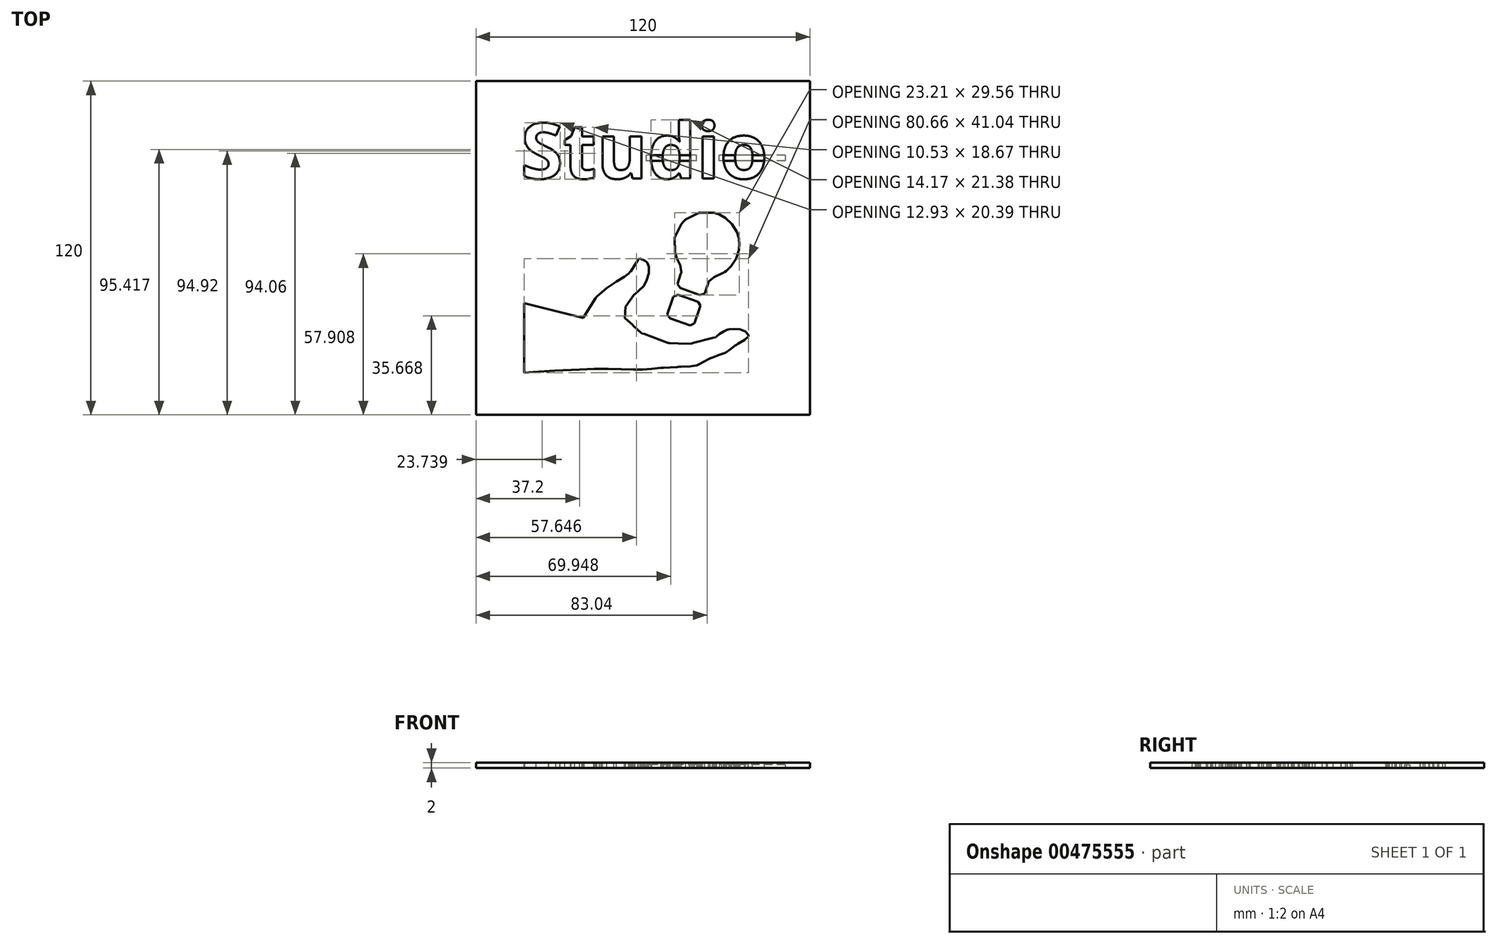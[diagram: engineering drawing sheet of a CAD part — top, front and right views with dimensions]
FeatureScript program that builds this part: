
annotation { "Feature Type Name" : "Feature", "Feature Type Description" : "" }
export const myFeature = defineFeature(function(context is Context, id is Id, definition is map)
    precondition{}
    {
        {
            var Q0;
            Q0=qCreatedBy(makeId("Top.planeOp"),FACE);
            var sketch = newSketch(context, id + "F0", { "sketchPlane" : qUnion([Q0])});
            skLineSegment(sketch, "E0.bottom", {"start": v(-61, 60) * mm, "end": v(59, 60) * mm});
            skLineSegment(sketch, "E0.top", {"start": v(-61, -60) * mm, "end": v(59, -60) * mm});
            skLineSegment(sketch, "E0.left", {"start": v(-61, 60) * mm, "end": v(-61, -60) * mm});
            skLineSegment(sketch, "E0.right", {"start": v(59, 60) * mm, "end": v(59, -60) * mm});
            skSolve(sketch);
        }
        {
            var Q0;
            Q0=qSketchRegion(id+"F0",true);
            extrude(context, id + "F1", {"entities" : qUnion([Q0]), "depth" : 2 * mm});
        }
        {
            var Q0;
            Q0=makeQuery(id+"F1.opExtrude","CAP_FACE",FACE,{"disambiguationData":[OSD([sQuery(id+"F0.wireOp",EDGE,"E0.bottom"),sQuery(id+"F0.wireOp",EDGE,"E0.top"),sQuery(id+"F0.wireOp",EDGE,"E0.left"),sQuery(id+"F0.wireOp",EDGE,"E0.right")])],"isStart":false});
            var sketch = newSketch(context, id + "F2", { "sketchPlane" : qUnion([Q0])});
            skText(sketch, "E1", { "text": "Studio", "fontName": "OpenSans-Bold.ttf"});
            const initialGuessF2  = {"E1": [-0.045, 0.025, 1, 0, 0.02]};
            skSetInitialGuess(sketch, initialGuessF2);
            skSolve(sketch);
        }
        {
            var Q0;
            Q0=qSketchRegion(id+"F2",true);
            extrude(context, id + "F3", {"entities" : qUnion([Q0]), "operationType" : NewBodyOperationType.REMOVE, "oppositeDirection" : true, "depth" : 25 * mm});
        }
        {
            var Q0;
            {var subQ0=sQuery(id+"F0.wireOp",EDGE,"E0.top");var subQ1=sQuery(id+"F0.wireOp",EDGE,"E0.right");var subQ2=sQuery(id+"F0.wireOp",EDGE,"E0.bottom");var subQ3=sQuery(id+"F0.wireOp",EDGE,"E0.left");Q0=makeQuery(id+"F3.boolean.opBoolean","SPLIT",FACE,{"disambiguationData":[TD([makeQuery(id+"F1.opExtrude","SWEPT_FACE",FACE,{"disambiguationData":[OSD([subQ2])]})])],"derivedFrom":makeQuery(id+"F1.opExtrude","CAP_FACE",FACE,{"disambiguationData":[OSD([subQ2,subQ0,subQ3,subQ1])],"isStart":false})});}
            var sketch = newSketch(context, id + "F4", { "sketchPlane" : qUnion([Q0])});
            skLineSegment(sketch, "E2", {"start": v(-43.68, -19.85) * mm, "end": v(-43.68, -44.85) * mm});
            skLineSegment(sketch, "E3", {"start": v(-43.68, -44.85) * mm, "end": v(-40.4, -44.62) * mm});
            skLineSegment(sketch, "E4", {"start": v(-40.4, -44.62) * mm, "end": v(-32.66, -44.12) * mm});
            skLineSegment(sketch, "E5", {"start": v(-32.66, -44.12) * mm, "end": v(-23.76, -43.64) * mm});
            skLineSegment(sketch, "E6", {"start": v(-23.76, -43.64) * mm, "end": v(-18.48, -43.42) * mm});
            skLineSegment(sketch, "E7", {"start": v(-18.48, -43.42) * mm, "end": v(-16.9, -43.43) * mm});
            skLineSegment(sketch, "E8", {"start": v(-16.9, -43.43) * mm, "end": v(-16.04, -43.43) * mm});
            skLineSegment(sketch, "E9", {"start": v(-16.04, -43.43) * mm, "end": v(-13.48, -43.48) * mm});
            skLineSegment(sketch, "E10", {"start": v(-13.48, -43.48) * mm, "end": v(-8.78, -43.57) * mm});
            skLineSegment(sketch, "E11", {"start": v(-8.78, -43.57) * mm, "end": v(-4.34, -43.65) * mm});
            skLineSegment(sketch, "E12", {"start": v(-4.34, -43.65) * mm, "end": v(-2.09, -43.67) * mm});
            skLineSegment(sketch, "E13", {"start": v(-2.09, -43.67) * mm, "end": v(-1.65, -43.66) * mm});
            skLineSegment(sketch, "E14", {"start": v(-1.65, -43.66) * mm, "end": v(-1.15, -43.64) * mm});
            skLineSegment(sketch, "E15", {"start": v(-1.15, -43.64) * mm, "end": v(2.17, -43.39) * mm});
            skLineSegment(sketch, "E16", {"start": v(2.17, -43.39) * mm, "end": v(5.45, -43.1) * mm});
            skLineSegment(sketch, "E17", {"start": v(5.45, -43.1) * mm, "end": v(5.93, -43.06) * mm});
            skLineSegment(sketch, "E18", {"start": v(5.93, -43.06) * mm, "end": v(6.4, -43.02) * mm});
            skLineSegment(sketch, "E19", {"start": v(6.4, -43.02) * mm, "end": v(8.69, -42.9) * mm});
            skLineSegment(sketch, "E20", {"start": v(8.69, -42.9) * mm, "end": v(11.26, -42.76) * mm});
            skLineSegment(sketch, "E21", {"start": v(11.26, -42.76) * mm, "end": v(11.88, -42.72) * mm});
            skLineSegment(sketch, "E22", {"start": v(11.88, -42.72) * mm, "end": v(12.7, -42.65) * mm});
            skLineSegment(sketch, "E23", {"start": v(12.7, -42.65) * mm, "end": v(15.93, -42.51) * mm});
            skLineSegment(sketch, "E24", {"start": v(15.93, -42.51) * mm, "end": v(18.43, -42.11) * mm});
            skLineSegment(sketch, "E25", {"start": v(18.43, -42.11) * mm, "end": v(18.89, -41.92) * mm});
            skLineSegment(sketch, "E26", {"start": v(18.89, -41.92) * mm, "end": v(19.2, -41.79) * mm});
            skLineSegment(sketch, "E27", {"start": v(19.2, -41.79) * mm, "end": v(20.81, -40.9) * mm});
            skLineSegment(sketch, "E28", {"start": v(20.81, -40.9) * mm, "end": v(22.77, -39.85) * mm});
            skLineSegment(sketch, "E29", {"start": v(22.77, -39.85) * mm, "end": v(23.24, -39.65) * mm});
            skLineSegment(sketch, "E30", {"start": v(23.24, -39.65) * mm, "end": v(23.92, -39.34) * mm});
            skLineSegment(sketch, "E31", {"start": v(23.92, -39.34) * mm, "end": v(26.56, -38.33) * mm});
            skLineSegment(sketch, "E32", {"start": v(26.56, -38.33) * mm, "end": v(28.37, -37.7) * mm});
            skLineSegment(sketch, "E33", {"start": v(28.37, -37.7) * mm, "end": v(28.64, -37.59) * mm});
            skLineSegment(sketch, "E34", {"start": v(28.64, -37.59) * mm, "end": v(28.9, -37.46) * mm});
            skLineSegment(sketch, "E35", {"start": v(28.9, -37.46) * mm, "end": v(30.31, -36.44) * mm});
            skLineSegment(sketch, "E36", {"start": v(30.31, -36.44) * mm, "end": v(32.13, -35.05) * mm});
            skLineSegment(sketch, "E37", {"start": v(32.13, -35.05) * mm, "end": v(32.6, -34.75) * mm});
            skLineSegment(sketch, "E38", {"start": v(32.6, -34.75) * mm, "end": v(33.06, -34.44) * mm});
            skLineSegment(sketch, "E39", {"start": v(33.06, -34.44) * mm, "end": v(35.54, -32.97) * mm});
            skLineSegment(sketch, "E40", {"start": v(35.54, -32.97) * mm, "end": v(36.98, -31.77) * mm});
            skLineSegment(sketch, "E41", {"start": v(36.98, -31.77) * mm, "end": v(36.92, -31.6) * mm});
            skLineSegment(sketch, "E42", {"start": v(36.92, -31.6) * mm, "end": v(36.75, -31.13) * mm});
            skLineSegment(sketch, "E43", {"start": v(36.75, -31.13) * mm, "end": v(35.73, -29.93) * mm});
            skLineSegment(sketch, "E44", {"start": v(35.73, -29.93) * mm, "end": v(33.88, -29.17) * mm});
            skLineSegment(sketch, "E45", {"start": v(33.88, -29.17) * mm, "end": v(31.66, -29.06) * mm});
            skLineSegment(sketch, "E46", {"start": v(31.66, -29.06) * mm, "end": v(29.93, -29.27) * mm});
            skLineSegment(sketch, "E47", {"start": v(29.93, -29.27) * mm, "end": v(29.37, -29.38) * mm});
            skLineSegment(sketch, "E48", {"start": v(29.37, -29.38) * mm, "end": v(29, -29.45) * mm});
            skLineSegment(sketch, "E49", {"start": v(29, -29.45) * mm, "end": v(28, -29.95) * mm});
            skLineSegment(sketch, "E50", {"start": v(28, -29.95) * mm, "end": v(26.57, -30.9) * mm});
            skLineSegment(sketch, "E51", {"start": v(26.57, -30.9) * mm, "end": v(25.44, -31.77) * mm});
            skLineSegment(sketch, "E52", {"start": v(25.44, -31.77) * mm, "end": v(24.98, -32.17) * mm});
            skLineSegment(sketch, "E53", {"start": v(24.98, -32.17) * mm, "end": v(24.27, -32.3) * mm});
            skLineSegment(sketch, "E54", {"start": v(24.27, -32.3) * mm, "end": v(17.3, -34.1) * mm});
            skLineSegment(sketch, "E55", {"start": v(17.3, -34.1) * mm, "end": v(16.62, -34.34) * mm});
            skLineSegment(sketch, "E56", {"start": v(16.62, -34.34) * mm, "end": v(15.73, -34.41) * mm});
            skLineSegment(sketch, "E57", {"start": v(15.73, -34.41) * mm, "end": v(11.68, -34.32) * mm});
            skLineSegment(sketch, "E58", {"start": v(11.68, -34.32) * mm, "end": v(8.64, -34.18) * mm});
            skLineSegment(sketch, "E59", {"start": v(8.64, -34.18) * mm, "end": v(8.28, -34.23) * mm});
            skLineSegment(sketch, "E60", {"start": v(8.28, -34.23) * mm, "end": v(7.5, -33.86) * mm});
            skLineSegment(sketch, "E61", {"start": v(7.5, -33.86) * mm, "end": v(-0.5, -30.92) * mm});
            skLineSegment(sketch, "E62", {"start": v(-0.5, -30.92) * mm, "end": v(-1.32, -30.7) * mm});
            skLineSegment(sketch, "E63", {"start": v(-1.32, -30.7) * mm, "end": v(-1.63, -30.5) * mm});
            skLineSegment(sketch, "E64", {"start": v(-1.63, -30.5) * mm, "end": v(-4.31, -28.1) * mm});
            skLineSegment(sketch, "E65", {"start": v(-4.31, -28.1) * mm, "end": v(-4.54, -27.82) * mm});
            skLineSegment(sketch, "E66", {"start": v(-4.54, -27.82) * mm, "end": v(-4.75, -27.56) * mm});
            skLineSegment(sketch, "E67", {"start": v(-4.75, -27.56) * mm, "end": v(-7.25, -25.36) * mm});
            skLineSegment(sketch, "E68", {"start": v(-7.25, -25.36) * mm, "end": v(-7.54, -25.2) * mm});
            skLineSegment(sketch, "E69", {"start": v(-7.54, -25.2) * mm, "end": v(-7.3, -21.13) * mm});
            skLineSegment(sketch, "E70", {"start": v(-7.3, -21.13) * mm, "end": v(-4.22, -16.71) * mm});
            skLineSegment(sketch, "E71", {"start": v(-4.22, -16.71) * mm, "end": v(-3.88, -16.5) * mm});
            skLineSegment(sketch, "E72", {"start": v(-3.88, -16.5) * mm, "end": v(-0.9, -13.9) * mm});
            skLineSegment(sketch, "E73", {"start": v(-0.9, -13.9) * mm, "end": v(-0.65, -13.6) * mm});
            skLineSegment(sketch, "E74", {"start": v(-0.65, -13.6) * mm, "end": v(-0.35, -13.09) * mm});
            skLineSegment(sketch, "E75", {"start": v(-0.35, -13.09) * mm, "end": v(0.4, -11.46) * mm});
            skLineSegment(sketch, "E76", {"start": v(0.4, -11.46) * mm, "end": v(1.1, -9.04) * mm});
            skLineSegment(sketch, "E77", {"start": v(1.1, -9.04) * mm, "end": v(1.14, -6.74) * mm});
            skLineSegment(sketch, "E78", {"start": v(1.14, -6.74) * mm, "end": v(0.56, -5.3) * mm});
            skLineSegment(sketch, "E79", {"start": v(0.56, -5.3) * mm, "end": v(0.21, -5) * mm});
            skLineSegment(sketch, "E80", {"start": v(0.21, -5) * mm, "end": v(-0.25, -4.6) * mm});
            skLineSegment(sketch, "E81", {"start": v(-0.25, -4.6) * mm, "end": v(-1.97, -3.81) * mm});
            skLineSegment(sketch, "E82", {"start": v(-1.97, -3.81) * mm, "end": v(-2.63, -3.97) * mm});
            skLineSegment(sketch, "E83", {"start": v(-2.63, -3.97) * mm, "end": v(-2.84, -4.39) * mm});
            skLineSegment(sketch, "E84", {"start": v(-2.84, -4.39) * mm, "end": v(-5.4, -8.34) * mm});
            skLineSegment(sketch, "E85", {"start": v(-5.4, -8.34) * mm, "end": v(-5.7, -8.7) * mm});
            skLineSegment(sketch, "E86", {"start": v(-5.7, -8.7) * mm, "end": v(-6.1, -9.16) * mm});
            skLineSegment(sketch, "E87", {"start": v(-6.1, -9.16) * mm, "end": v(-7.65, -10.26) * mm});
            skLineSegment(sketch, "E88", {"start": v(-7.65, -10.26) * mm, "end": v(-10.55, -12.06) * mm});
            skLineSegment(sketch, "E89", {"start": v(-10.55, -12.06) * mm, "end": v(-13.98, -14.38) * mm});
            skLineSegment(sketch, "E90", {"start": v(-13.98, -14.38) * mm, "end": v(-16.7, -16.62) * mm});
            skLineSegment(sketch, "E91", {"start": v(-16.7, -16.62) * mm, "end": v(-17.51, -17.46) * mm});
            skLineSegment(sketch, "E92", {"start": v(-17.51, -17.46) * mm, "end": v(-18.04, -18.02) * mm});
            skLineSegment(sketch, "E93", {"start": v(-18.04, -18.02) * mm, "end": v(-22.14, -24.49) * mm});
            skLineSegment(sketch, "E94", {"start": v(-22.14, -24.49) * mm, "end": v(-22.43, -25.2) * mm});
            skLineSegment(sketch, "E95", {"start": v(-22.43, -25.2) * mm, "end": v(-43.68, -19.85) * mm});
            skLineSegment(sketch, "E96", {"start": v(19.65, -20.77) * mm, "end": v(17.48, -27.11) * mm});
            skLineSegment(sketch, "E97", {"start": v(17.48, -27.11) * mm, "end": v(15.95, -27.8) * mm});
            skLineSegment(sketch, "E98", {"start": v(15.95, -27.8) * mm, "end": v(8.75, -25.34) * mm});
            skLineSegment(sketch, "E99", {"start": v(8.75, -25.34) * mm, "end": v(7.74, -23.9) * mm});
            skLineSegment(sketch, "E100", {"start": v(7.74, -23.9) * mm, "end": v(9.9, -17.6) * mm});
            skLineSegment(sketch, "E101", {"start": v(9.9, -17.6) * mm, "end": v(11.5, -16.8) * mm});
            skLineSegment(sketch, "E102", {"start": v(11.5, -16.8) * mm, "end": v(18.78, -19.28) * mm});
            skLineSegment(sketch, "E103", {"start": v(18.78, -19.28) * mm, "end": v(19.65, -20.77) * mm});
            skLineSegment(sketch, "E104", {"start": v(28.23, -8.67) * mm, "end": v(28.92, -8.22) * mm});
            skLineSegment(sketch, "E105", {"start": v(28.92, -8.22) * mm, "end": v(30.73, -6.5) * mm});
            skLineSegment(sketch, "E106", {"start": v(30.73, -6.5) * mm, "end": v(32.51, -3.78) * mm});
            skLineSegment(sketch, "E107", {"start": v(32.51, -3.78) * mm, "end": v(33.48, -0.68) * mm});
            skLineSegment(sketch, "E108", {"start": v(33.48, -0.68) * mm, "end": v(33.64, 1.82) * mm});
            skLineSegment(sketch, "E109", {"start": v(33.64, 1.82) * mm, "end": v(33.55, 2.63) * mm});
            skLineSegment(sketch, "E110", {"start": v(33.55, 2.63) * mm, "end": v(33.45, 3.44) * mm});
            skLineSegment(sketch, "E111", {"start": v(33.45, 3.44) * mm, "end": v(32.68, 5.83) * mm});
            skLineSegment(sketch, "E112", {"start": v(32.68, 5.83) * mm, "end": v(31, 8.6) * mm});
            skLineSegment(sketch, "E113", {"start": v(31, 8.6) * mm, "end": v(28.64, 10.83) * mm});
            skLineSegment(sketch, "E114", {"start": v(28.64, 10.83) * mm, "end": v(26.46, 12.06) * mm});
            skLineSegment(sketch, "E115", {"start": v(26.46, 12.06) * mm, "end": v(25.69, 12.32) * mm});
            skLineSegment(sketch, "E116", {"start": v(25.69, 12.32) * mm, "end": v(24.62, 12.69) * mm});
            skLineSegment(sketch, "E117", {"start": v(24.62, 12.69) * mm, "end": v(19.2, 12.64) * mm});
            skLineSegment(sketch, "E118", {"start": v(19.2, 12.64) * mm, "end": v(14.33, 10.26) * mm});
            skLineSegment(sketch, "E119", {"start": v(14.33, 10.26) * mm, "end": v(13.54, 9.46) * mm});
            skLineSegment(sketch, "E120", {"start": v(13.54, 9.46) * mm, "end": v(12.75, 8.66) * mm});
            skLineSegment(sketch, "E121", {"start": v(12.75, 8.66) * mm, "end": v(10.43, 3.76) * mm});
            skLineSegment(sketch, "E122", {"start": v(10.43, 3.76) * mm, "end": v(10.46, -1.66) * mm});
            skLineSegment(sketch, "E123", {"start": v(10.46, -1.66) * mm, "end": v(10.84, -2.72) * mm});
            skLineSegment(sketch, "E124", {"start": v(10.84, -2.72) * mm, "end": v(10.97, -3.15) * mm});
            skLineSegment(sketch, "E125", {"start": v(10.97, -3.15) * mm, "end": v(11.19, -3.7) * mm});
            skLineSegment(sketch, "E126", {"start": v(11.19, -3.7) * mm, "end": v(12.38, -6.24) * mm});
            skLineSegment(sketch, "E127", {"start": v(12.38, -6.24) * mm, "end": v(12.77, -8.76) * mm});
            skLineSegment(sketch, "E128", {"start": v(12.77, -8.76) * mm, "end": v(12.6, -9.3) * mm});
            skLineSegment(sketch, "E129", {"start": v(12.6, -9.3) * mm, "end": v(11.36, -12.98) * mm});
            skLineSegment(sketch, "E130", {"start": v(11.36, -12.98) * mm, "end": v(12.37, -14.42) * mm});
            skLineSegment(sketch, "E131", {"start": v(12.37, -14.42) * mm, "end": v(19.4, -16.87) * mm});
            skLineSegment(sketch, "E132", {"start": v(19.4, -16.87) * mm, "end": v(21.2, -16.4) * mm});
            skLineSegment(sketch, "E133", {"start": v(21.2, -16.4) * mm, "end": v(22.43, -12.63) * mm});
            skLineSegment(sketch, "E134", {"start": v(22.43, -12.63) * mm, "end": v(22.6, -12.1) * mm});
            skLineSegment(sketch, "E135", {"start": v(22.6, -12.1) * mm, "end": v(24.6, -10.43) * mm});
            skLineSegment(sketch, "E136", {"start": v(24.6, -10.43) * mm, "end": v(27.34, -9.17) * mm});
            skLineSegment(sketch, "E137", {"start": v(27.34, -9.17) * mm, "end": v(27.9, -8.84) * mm});
            skLineSegment(sketch, "E138", {"start": v(27.9, -8.84) * mm, "end": v(28.23, -8.67) * mm});
            skSolve(sketch);
        }
        {
            var Q0;
            Q0 = qSketchRegion(id + "F4", true);
            extrude(context, id + "F5", {"entities" : qUnion([Q0]), "operationType" : NewBodyOperationType.REMOVE, "oppositeDirection" : true, "depth" : 25 * mm});
        }
        {
            var Q0;
            {var subQ0=sQuery(id+"F0.wireOp",EDGE,"E0.top");var subQ1=sQuery(id+"F0.wireOp",EDGE,"E0.right");var subQ2=sQuery(id+"F0.wireOp",EDGE,"E0.bottom");var subQ3=sQuery(id+"F0.wireOp",EDGE,"E0.left");Q0=makeQuery(id+"F3.boolean.opBoolean","SPLIT",FACE,{"disambiguationData":[TD([makeQuery(id+"F1.opExtrude","SWEPT_FACE",FACE,{"disambiguationData":[OSD([subQ2])]})])],"derivedFrom":makeQuery(id+"F1.opExtrude","CAP_FACE",FACE,{"disambiguationData":[OSD([subQ2,subQ0,subQ3,subQ1])],"isStart":true})});}
            var sketch = newSketch(context, id + "F6", { "sketchPlane" : qUnion([Q0])});
            skLineSegment(sketch, "E139.bottom", {"start": v(50.12, -33.37) * mm, "end": v(26.38, -33.37) * mm});
            skLineSegment(sketch, "E139.top", {"start": v(50.12, -31.37) * mm, "end": v(26.38, -31.37) * mm});
            skLineSegment(sketch, "E139.left", {"start": v(50.12, -33.37) * mm, "end": v(50.12, -31.37) * mm});
            skLineSegment(sketch, "E139.right", {"start": v(0.12, -33.37) * mm, "end": v(0.12, -31.37) * mm});
            skLineSegment(sketch, "E140", {"start": v(18.2, -31.37) * mm, "end": v(18.2, -33.37) * mm});
            skLineSegment(sketch, "E141", {"start": v(26.38, -31.37) * mm, "end": v(26.38, -33.37) * mm});
            skLineSegment(sketch, "E142.trimOffspring", {"start": v(18.2, -31.37) * mm, "end": v(0.12, -31.37) * mm});
            skLineSegment(sketch, "E143.trimOffspring", {"start": v(18.2, -33.37) * mm, "end": v(0.12, -33.37) * mm});
            skSolve(sketch);
        }
        {
            var Q0;
            Q0 = qSketchRegion(id + "F6", true);
            extrude(context, id + "F7", {"entities" : qUnion([Q0]), "oppositeDirection" : true, "depth" : 1.2 * mm});
        }
    });
